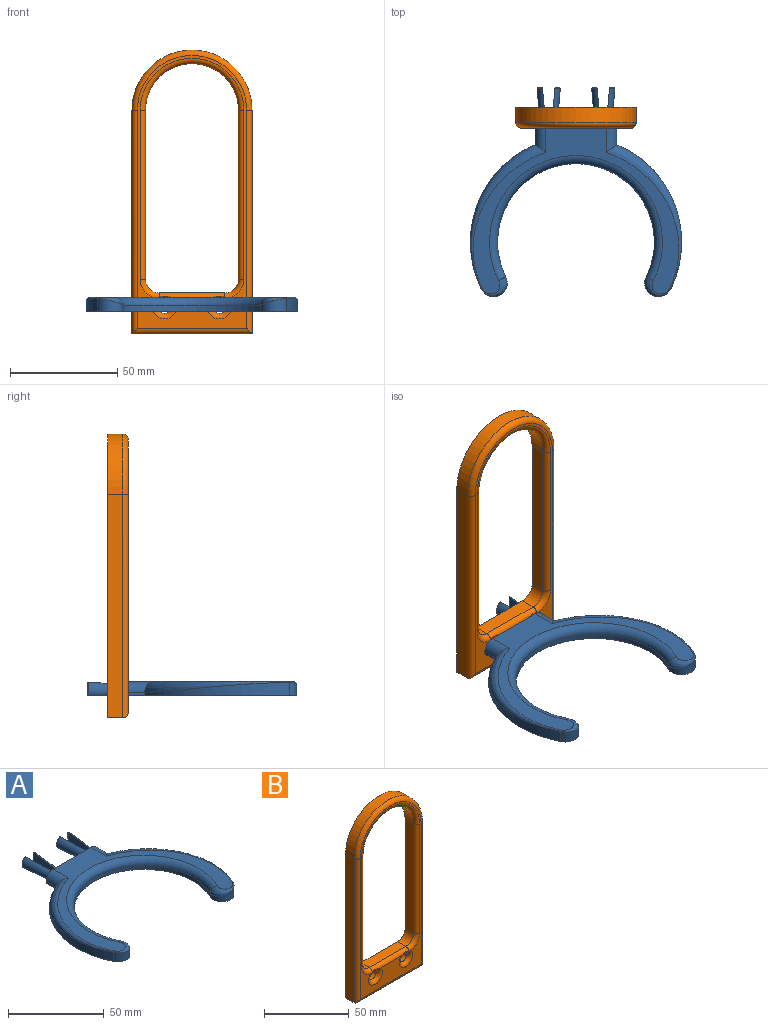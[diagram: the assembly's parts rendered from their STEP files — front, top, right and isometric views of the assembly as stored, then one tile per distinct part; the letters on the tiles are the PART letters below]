
ASSEMBLY  parts=2 mates=1
PART A: 49 faces, bbox 98.7x101.5x9.6 mm
  f0: bspline ~16.98x7.36mm, area 115.6mm2, adj f4,f6,f12,f39
  f1: plane 4.73x1.27mm, normal (0,1,0), area 4.5mm2, adj f10,f11,f39
  f2: bspline ~22.86x9.42mm, area 115.6mm2, adj f5,f8,f11,f39
  f3: plane 4.73x1.27mm, normal (0,1,0), area 4.5mm2, adj f12,f13,f39
  f4: plane 17.43x6.08mm, normal (1,0.09,0), area 95.4mm2, adj f0,f6,f7,f12,f13,f39
  f5: plane 17.43x6.08mm, normal (-1,0.09,0), area 95.4mm2, adj f2,f8,f9,f10,f11,f39
  f6: bspline ~7.95x5.81mm, area 15.6mm2, adj f0,f4,f7,f29,f38,f39
  f7: cylinder r=1.27mm len=6.35mm, axis (0,0,-1), area 10.5mm2, adj f4,f6,f31,f38,f39
  f8: bspline ~8.06x6.02mm, area 15.6mm2, adj f2,f5,f9,f32,f38,f39
  f9: cylinder r=1.27mm len=6.35mm, axis (0,0,-1), area 10.5mm2, adj f5,f8,f31,f38,f39
  f10: cylinder r=0.64mm len=5.96mm, axis (0,0,-1), area 5mm2, adj f1,f5,f11,f39
  f11: bspline ~7.68x3.99mm, area 6.7mm2, adj f1,f2,f5,f10,f39
  f12: bspline ~7.47x3.41mm, area 6.7mm2, adj f0,f3,f4,f13,f39
  f13: cylinder r=0.64mm len=5.96mm, axis (0,0,-1), area 5mm2, adj f3,f4,f12,f39
  f14: bspline ~7.68x3.99mm, area 6.7mm2, adj f15,f18,f19,f20,f39
  f15: cylinder r=0.64mm len=5.96mm, axis (0,0,-1), area 5mm2, adj f14,f18,f20,f39
  f16: cylinder r=1.27mm len=6.35mm, axis (0,0,-1), area 10.5mm2, adj f17,f18,f28,f38,f39
  f17: bspline ~8.06x6.02mm, area 15.6mm2, adj f16,f18,f19,f30,f38,f39
  f18: plane 17.43x6.08mm, normal (1,0.09,0), area 95.4mm2, adj f14,f15,f16,f17,f19,f39
  f19: bspline ~22.86x9.42mm, area 115.6mm2, adj f14,f17,f18,f39
  f20: plane 4.73x1.27mm, normal (0,1,0), area 4.5mm2, adj f14,f15,f39
  f21: bspline ~16.98x7.36mm, area 115.6mm2, adj f23,f24,f26,f39
  f22: plane 4.73x1.27mm, normal (0,1,0), area 4.5mm2, adj f26,f27,f39
  f23: plane 17.43x6.08mm, normal (-1,0.09,0), area 95.4mm2, adj f21,f24,f25,f26,f27,f39
  f24: bspline ~7.95x5.81mm, area 15.6mm2, adj f21,f23,f25,f29,f38,f39
  f25: cylinder r=1.27mm len=6.35mm, axis (0,0,-1), area 10.5mm2, adj f23,f24,f28,f38,f39
  f26: bspline ~7.33x3.41mm, area 6.7mm2, adj f21,f22,f23,f27,f39
  f27: cylinder r=0.64mm len=5.96mm, axis (0,0,-1), area 5mm2, adj f22,f23,f26,f39
  f28: plane 6.35x0.21mm, normal (0,1,0), area 1.3mm2, adj f16,f25,f38,f39
  f29: plane 23.07x6.36mm, normal (0,1,0), area 105mm2, adj f6,f24,f38,f39
  f30: plane 6.36x5.19mm, normal (0,1,0), area 6.6mm2, adj f17,f35,f38,f39,f48
  f31: plane 6.35x0.21mm, normal (0,1,0), area 1.3mm2, adj f7,f9,f38,f39
  f32: plane 6.36x5.19mm, normal (0,1,0), area 6.6mm2, adj f8,f34,f38,f39,f47
  f33: cylinder r=49.15mm len=67.21mm, axis (0,0,-1), area 285.7mm2, adj f34,f39,f41,f46
  f34: plane 7.68x1.27mm, normal (1,0,0), area 9.8mm2, adj f32,f33,f39,f47
  f35: plane 7.68x1.27mm, normal (-1,0,0), area 9.8mm2, adj f30,f36,f39,f48
  f36: cylinder r=49.15mm len=67.21mm, axis (0,0,-1), area 285.7mm2, adj f35,f39,f40,f42
  f37: cylinder r=36.45mm len=72.9mm, axis (0,0,-1), area 376.4mm2, adj f39,f40,f41,f44
  f38: plane 95.9x77.36mm, normal (0,0,1), area 1317.9mm2, adj f6,f7,f8,f9,f16,f17,f24,f25
  f39: plane 98.51x97.68mm, normal (0,0,-1), area 2683.5mm2, adj f0,f1,f2,f3,f4,f5,f6,f7
  f40: cylinder r=6.35mm len=12.03mm, axis (0,0,-1), area 83.6mm2, adj f36,f37,f39,f43
  f41: cylinder r=6.35mm len=12.03mm, axis (0,0,-1), area 83.6mm2, adj f33,f37,f39,f45
  f42: bspline ~68.62x35.53mm, area 353mm2, adj f36,f38,f43,f48
  f43: bspline ~12.08x9.22mm, area 57mm2, adj f38,f40,f42,f44
  f44: torus R=40.26mm, axis (0,0,1), area 920.5mm2, adj f37,f38,f43,f45
  f45: bspline ~12.08x9.18mm, area 57.1mm2, adj f38,f41,f44,f46
  f46: bspline ~68.62x35.53mm, area 352.7mm2, adj f33,f38,f45,f47
  f47: cylinder r=5.08mm len=11.2mm, axis (0,-1,0), area 75.3mm2, adj f32,f34,f38,f46
  f48: cylinder r=5.08mm len=11.2mm, axis (0,1,0), area 75.3mm2, adj f30,f35,f38,f42
PART B: 26 faces, bbox 60.5x9.5x134.4 mm
  f0: cylinder r=27.94mm len=55.88mm, axis (0,1,0), area 613.1mm2, adj f1,f7,f11,f22
  f1: plane 104.14x6.99mm, normal (-1,0,0), area 727.4mm2, adj f0,f2,f11,f23
  f2: plane 55.88x6.99mm, normal (0,0,-1), area 390.3mm2, adj f1,f7,f11,f25
  f3: plane 78.74x6.99mm, normal (1,0,0), area 550mm2, adj f4,f11,f13,f20
  f4: cylinder r=21.59mm len=43.18mm, axis (0,1,0), area 473.8mm2, adj f3,f5,f11,f17
  f5: plane 78.74x6.99mm, normal (-1,0,0), area 550mm2, adj f4,f11,f12,f14
  f6: cylinder r=3.17mm len=6.99mm, axis (0,1,0), area 139.3mm2, adj f11,f19
  f7: plane 104.14x6.99mm, normal (1,0,0), area 727.4mm2, adj f0,f2,f11,f24
  f8: plane 30.48x6.99mm, normal (0,0,1), area 212.9mm2, adj f11,f12,f13,f18
  f9: cylinder r=3.17mm len=6.99mm, axis (0,1,0), area 139.3mm2, adj f11,f16
  f10: plane 127x50.8mm, normal (0,-1,0), area 882.1mm2, adj f14,f15,f16,f17,f18,f19,f20,f21
  f11: plane 132.08x55.88mm, normal (0,1,0), area 2593.2mm2, adj f0,f1,f2,f3,f4,f5,f6,f7
  f12: cylinder r=6.35mm len=6.99mm, axis (0,1,0), area 69.7mm2, adj f5,f8,f11,f15
  f13: cylinder r=6.35mm len=6.99mm, axis (0,-1,0), area 69.7mm2, adj f3,f8,f11,f21
  f14: cylinder r=2.54mm len=78.74mm, axis (0,0,1), area 314.2mm2, adj f5,f10,f15,f17
  f15: torus R=8.89mm, axis (0,-1,0), area 45mm2, adj f10,f12,f14,f16,f18
  f16: torus R=5.71mm, axis (0,-1,0), area 96.9mm2, adj f9,f10,f15,f18
  f17: torus R=24.13mm, axis (0,-1,0), area 282.2mm2, adj f4,f10,f14,f20
  f18: cylinder r=2.54mm len=30.48mm, axis (1,0,0), area 111.8mm2, adj f8,f10,f15,f16,f19,f21
  f19: torus R=5.71mm, axis (0,-1,0), area 96.9mm2, adj f6,f10,f18,f21
  f20: cylinder r=2.54mm len=78.74mm, axis (0,0,-1), area 314.2mm2, adj f3,f10,f17,f21
  f21: torus R=8.89mm, axis (0,-1,0), area 45mm2, adj f10,f13,f18,f19,f20
  f22: torus R=25.4mm, axis (0,-1,0), area 338.6mm2, adj f0,f10,f23,f24
  f23: cylinder r=2.54mm len=104.14mm, axis (0,0,1), area 411.8mm2, adj f1,f10,f22,f25
  f24: cylinder r=2.54mm len=104.14mm, axis (0,0,-1), area 411.8mm2, adj f7,f10,f22,f25
  f25: cylinder r=2.54mm len=55.88mm, axis (-1,0,0), area 215.6mm2, adj f2,f10,f23,f24
PLACE A t=(0,-65.69,-93.52)mm
PLACE B t=(0,-3.18,0)mm
MATE planar A.f29 <-> B.f10  axis (0,1,0) through (0,-12.7,-90.17)mm
